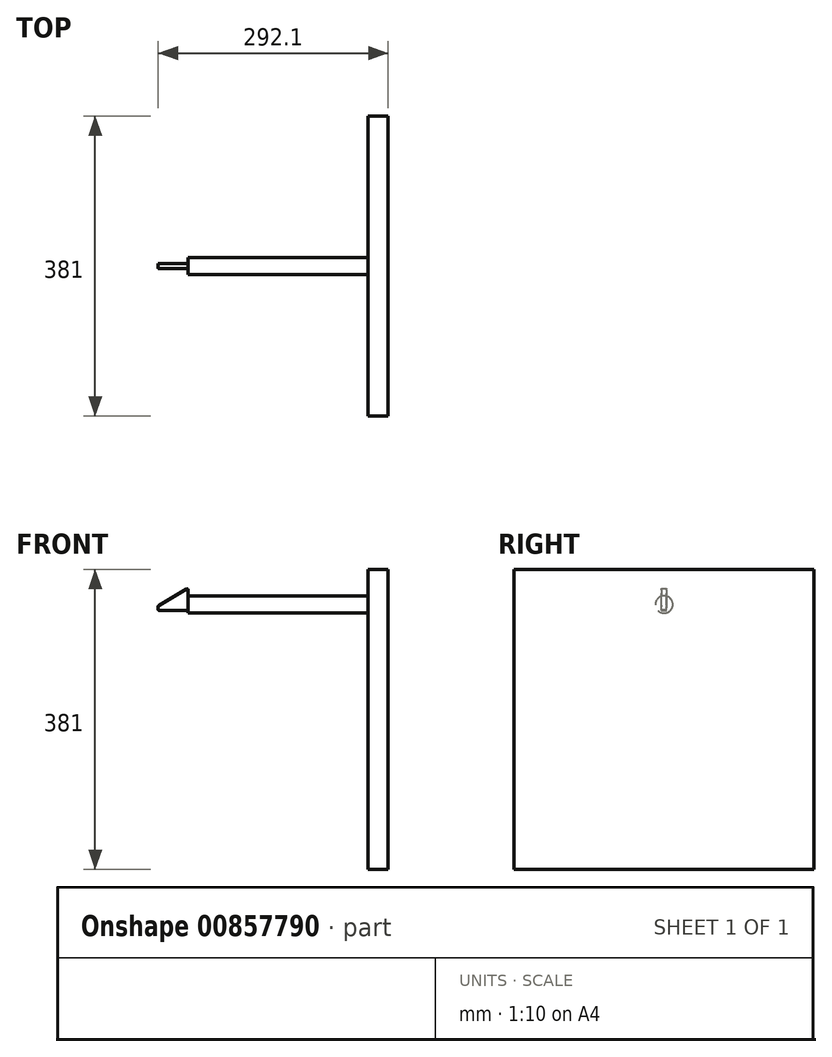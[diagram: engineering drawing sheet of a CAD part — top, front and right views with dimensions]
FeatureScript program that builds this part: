
annotation { "Feature Type Name" : "Feature", "Feature Type Description" : "" }
export const myFeature = defineFeature(function(context is Context, id is Id, definition is map)
    precondition{}
    {
        {
            var Q0;
            Q0=qCreatedBy(makeId("Front.planeOp"),FACE);
            var sketch = newSketch(context, id + "F0", { "sketchPlane" : qUnion([Q0])});
            skLineSegment(sketch, "E0", {"start": v(0, 18.53) * mm, "end": v(0, -6.22) * mm});
            skLineSegment(sketch, "E1", {"start": v(-1.52, -7.75) * mm, "end": v(-36.58, -7.75) * mm});
            skLineSegment(sketch, "E2", {"start": v(-38.1, -6.22) * mm, "end": v(-38.1, -2.26) * mm});
            skLineSegment(sketch, "E3", {"start": v(-37.35, -0.95) * mm, "end": v(-2.3, 19.84) * mm});
            skPoint(sketch, "E4.visualSharp", {"position": v(0, 21.2) * mm});
            skArc(sketch, "E4.filletArc", {"start": v(0, 18.53) * mm, "mid": v(-0.77, 19.86) * mm, "end": v(-2.3, 19.84) * mm});
            skPoint(sketch, "E5.visualSharp", {"position": v(0, -7.75) * mm});
            skArc(sketch, "E5.filletArc", {"start": v(-1.52, -7.75) * mm, "mid": v(-0.45, -7.3) * mm, "end": v(0, -6.22) * mm});
            skPoint(sketch, "E6.visualSharp", {"position": v(-38.1, -7.75) * mm});
            skArc(sketch, "E6.filletArc", {"start": v(-38.1, -6.22) * mm, "mid": v(-37.65, -7.3) * mm, "end": v(-36.58, -7.75) * mm});
            skPoint(sketch, "E7.visualSharp", {"position": v(-38.1, -1.4) * mm});
            skArc(sketch, "E7.filletArc", {"start": v(-37.35, -0.95) * mm, "mid": v(-37.9, -1.51) * mm, "end": v(-38.1, -2.26) * mm});
            skSolve(sketch);
        }
        {
            var Q0;
            Q0 = qSketchRegion(id + "F0", true);
            extrude(context, id + "F1", {"entities" : qUnion([Q0]), "depth" : 6.35 * mm, "offsetDistance" : 25.4 * mm, "symmetric" : true});
        }
        {
            var Q0;
            Q0=qCreatedBy(makeId("Right.planeOp"),FACE);
            var sketch = newSketch(context, id + "F2", { "sketchPlane" : qUnion([Q0])});
            skCircle(sketch, "E8", {"center": v(0, 0) * mm, "radius": 11.05 * mm});
            skSolve(sketch);
        }
        {
            var Q0;
            Q0 = qSketchRegion(id + "F2", true);
            extrude(context, id + "F3", {"entities" : qUnion([Q0]), "operationType" : NewBodyOperationType.ADD, "depth" : 228.6 * mm, "offsetDistance" : 25.4 * mm});
        }
        {
            var Q0;
            Q0=makeQuery(id+"F3.opExtrude","CAP_FACE",FACE,{"disambiguationData":[OSD([sQuery(id+"F2.wireOp",EDGE,"E8")])],"isStart":false});
            var sketch = newSketch(context, id + "F4", { "sketchPlane" : qUnion([Q0])});
            skLineSegment(sketch, "E9.bottom", {"start": v(-190.5, 44.45) * mm, "end": v(190.5, 44.45) * mm});
            skLineSegment(sketch, "E9.top", {"start": v(-190.5, -336.55) * mm, "end": v(190.5, -336.55) * mm});
            skLineSegment(sketch, "E9.left", {"start": v(-190.5, 44.45) * mm, "end": v(-190.5, -336.55) * mm});
            skLineSegment(sketch, "E9.right", {"start": v(190.5, 44.45) * mm, "end": v(190.5, -336.55) * mm});
            skSolve(sketch);
        }
        {
            var Q0;
            Q0 = qSketchRegion(id + "F4", true);
            extrude(context, id + "F5", {"entities" : qUnion([Q0]), "operationType" : NewBodyOperationType.ADD, "depth" : 25.4 * mm, "offsetDistance" : 25.4 * mm});
        }
    });
